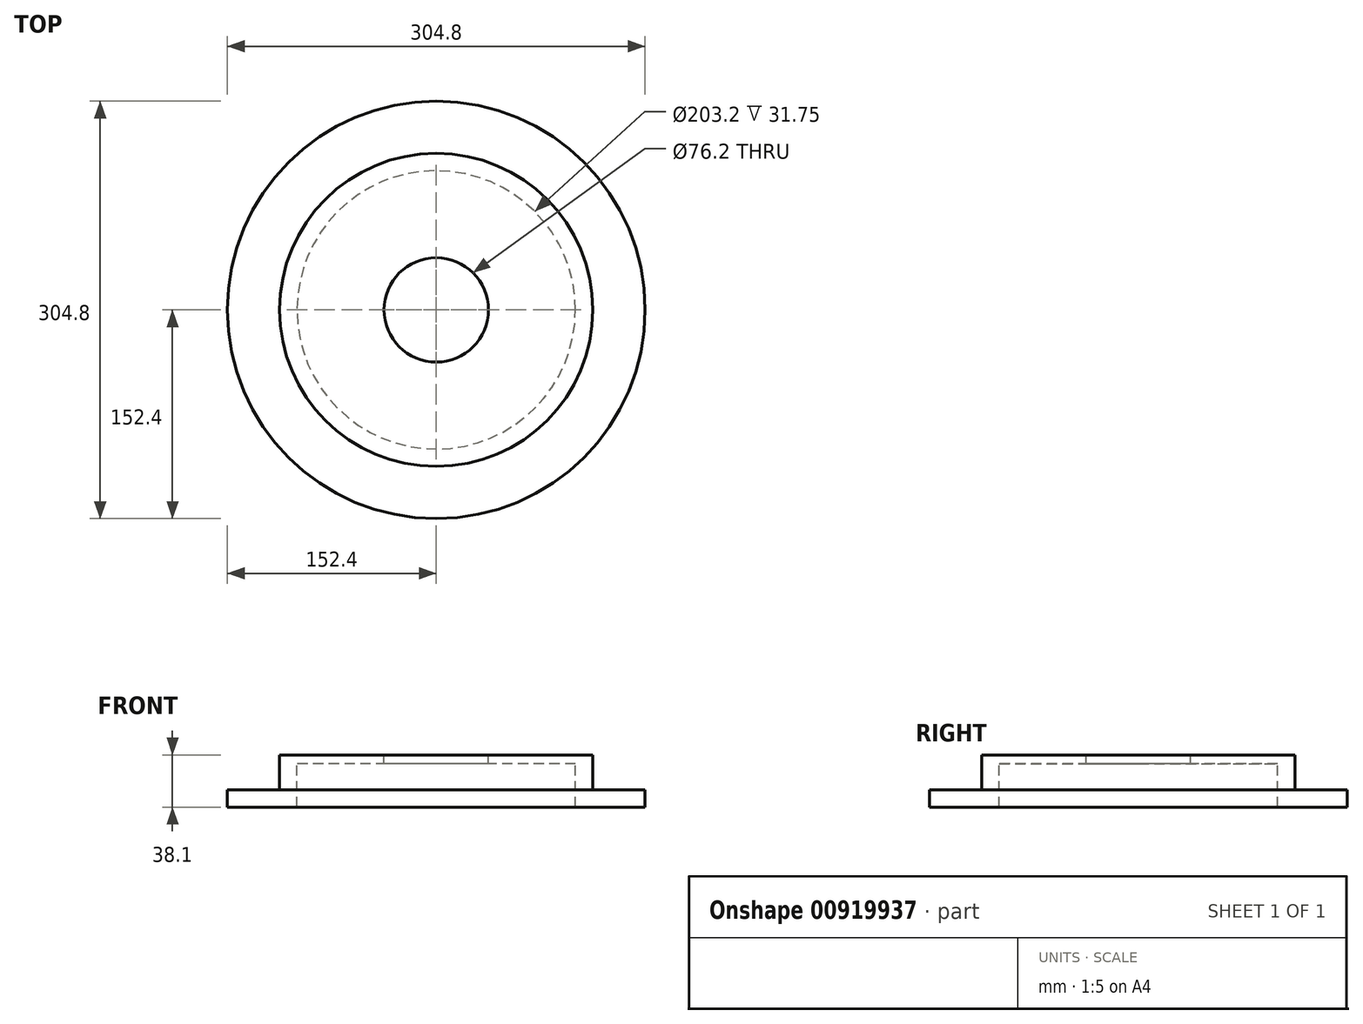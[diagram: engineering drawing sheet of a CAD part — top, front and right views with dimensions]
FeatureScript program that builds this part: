
annotation { "Feature Type Name" : "Feature", "Feature Type Description" : "" }
export const myFeature = defineFeature(function(context is Context, id is Id, definition is map)
    precondition{}
    {
        {
            var Q0;
            Q0=qCreatedBy(makeId("Front.planeOp"),FACE);
            var sketch = newSketch(context, id + "F0", { "sketchPlane" : qUnion([Q0])});
            skLineSegment(sketch, "E0", {"start": v(-101.6, 0) * mm, "end": v(-152.4, 0) * mm});
            skLineSegment(sketch, "E1", {"start": v(-152.4, 0) * mm, "end": v(-152.4, 12.7) * mm});
            skLineSegment(sketch, "E2", {"start": v(-152.4, 12.7) * mm, "end": v(-114.3, 12.7) * mm});
            skLineSegment(sketch, "E3", {"start": v(-114.3, 12.7) * mm, "end": v(-114.3, 38.1) * mm});
            skLineSegment(sketch, "E4", {"start": v(-114.3, 38.1) * mm, "end": v(-38.1, 38.1) * mm});
            skLineSegment(sketch, "E5", {"start": v(-38.1, 38.1) * mm, "end": v(-38.1, 31.75) * mm});
            skLineSegment(sketch, "E6", {"start": v(-38.1, 31.75) * mm, "end": v(-101.6, 31.75) * mm});
            skLineSegment(sketch, "E7", {"start": v(-101.6, 31.75) * mm, "end": v(-101.6, 0) * mm});
            skLineSegment(sketch, "E8", {"start": v(0, 0) * mm, "end": v(0, -144.13) * mm, "construction": true});
            skSolve(sketch);
        }
        {
            var Q0;
            Q0 = qSketchRegion(id + "F0", true);
            var Q1;
            Q1=sQuery(id+"F0.wireOp",EDGE,"E8");
            revolve(context, id + "F1", {"surfaceOperationType" : NewSurfaceOperationType.NEW, "entities" : qUnion([Q0]), "axis" : qUnion([Q1]), "revolveType" : RevolveType.FULL});
        }
    });
